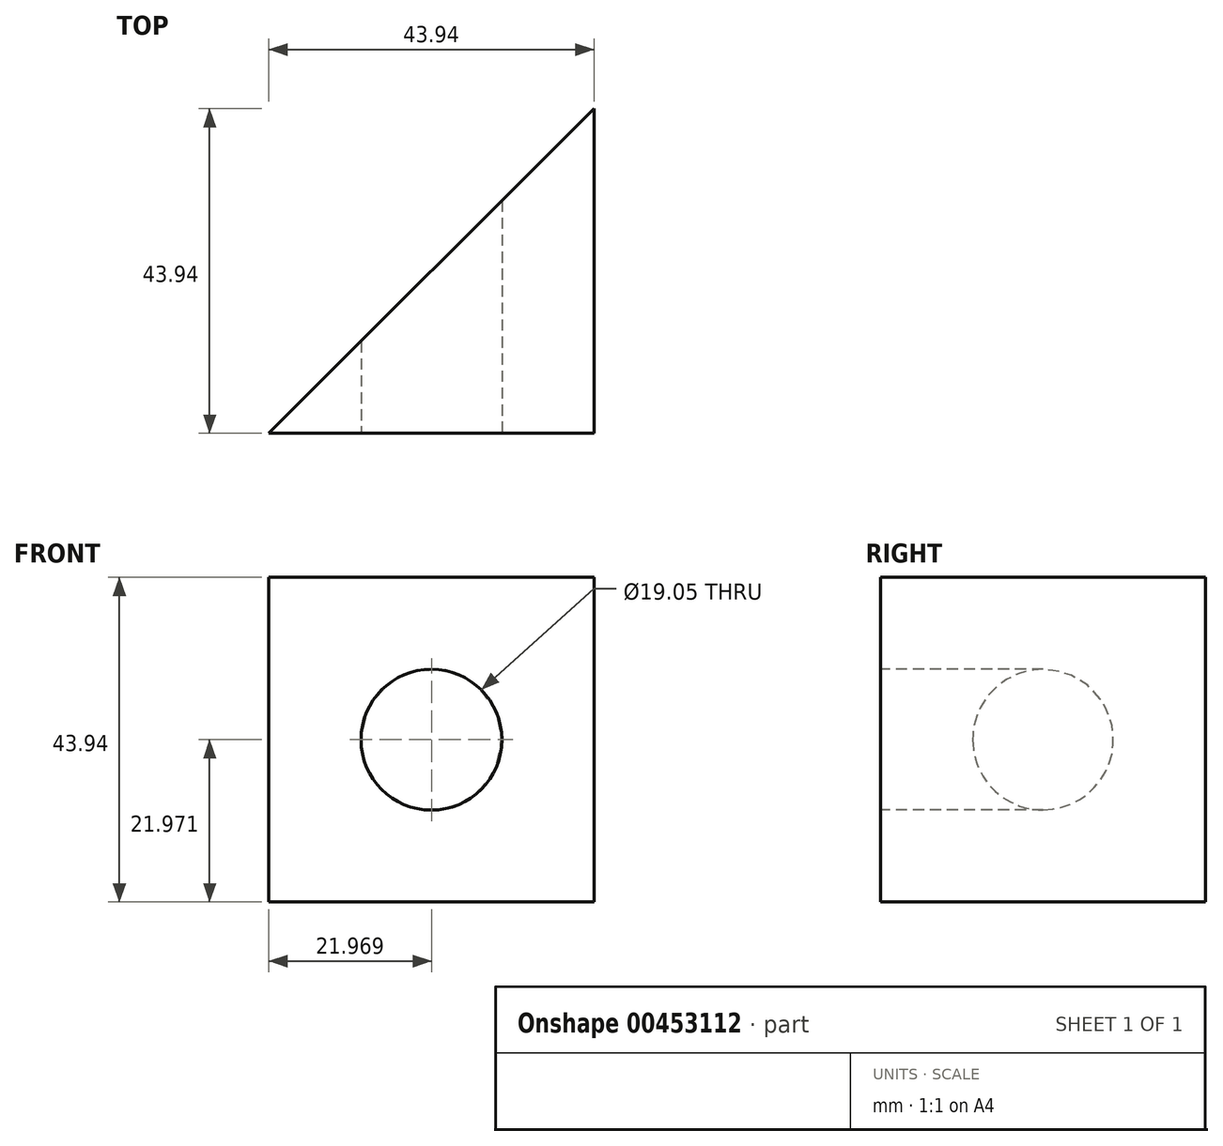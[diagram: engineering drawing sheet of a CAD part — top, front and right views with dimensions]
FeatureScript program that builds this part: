
annotation { "Feature Type Name" : "Feature", "Feature Type Description" : "" }
export const myFeature = defineFeature(function(context is Context, id is Id, definition is map)
    precondition{}
    {
        {
            var Q0;
            Q0=qCreatedBy(makeId("Top.planeOp"),FACE);
            var sketch = newSketch(context, id + "F0", { "sketchPlane" : qUnion([Q0])});
            skLineSegment(sketch, "E0", {"start": v(0, 0) * mm, "end": v(0, 43.94) * mm});
            skLineSegment(sketch, "E1", {"start": v(0, 43.94) * mm, "end": v(-43.94, 0) * mm});
            skLineSegment(sketch, "E2", {"start": v(-43.94, 0) * mm, "end": v(0, 0) * mm});
            skSolve(sketch);
        }
        {
            var Q0;
            Q0 = qSketchRegion(id + "F0", true);
            extrude(context, id + "F1", {"entities" : qUnion([Q0]), "depth" : 43.94 * mm});
        }
        {
            var Q0;
            Q0=makeQuery(id+"F1.opExtrude","SWEPT_FACE",FACE,{"disambiguationData":[OSD([sQuery(id+"F0.wireOp",EDGE,"E2")])]});
            var sketch = newSketch(context, id + "F2", { "sketchPlane" : qUnion([Q0])});
            skLineSegment(sketch, "E3", {"start": v(-21.97, 43.94) * mm, "end": v(-21.97, 0) * mm, "construction": true});
            skCircle(sketch, "E4", {"center": v(-21.97, 21.97) * mm, "radius": 9.53 * mm});
            skSolve(sketch);
        }
        {
            var Q0;
            Q0 = qSketchRegion(id + "F2", true);
            extrude(context, id + "F3", {"entities" : qUnion([Q0]), "operationType" : NewBodyOperationType.REMOVE, "endBound" : BoundingType.THROUGH_ALL, "oppositeDirection" : true, "depth" : 43.94 * mm});
        }
    });
